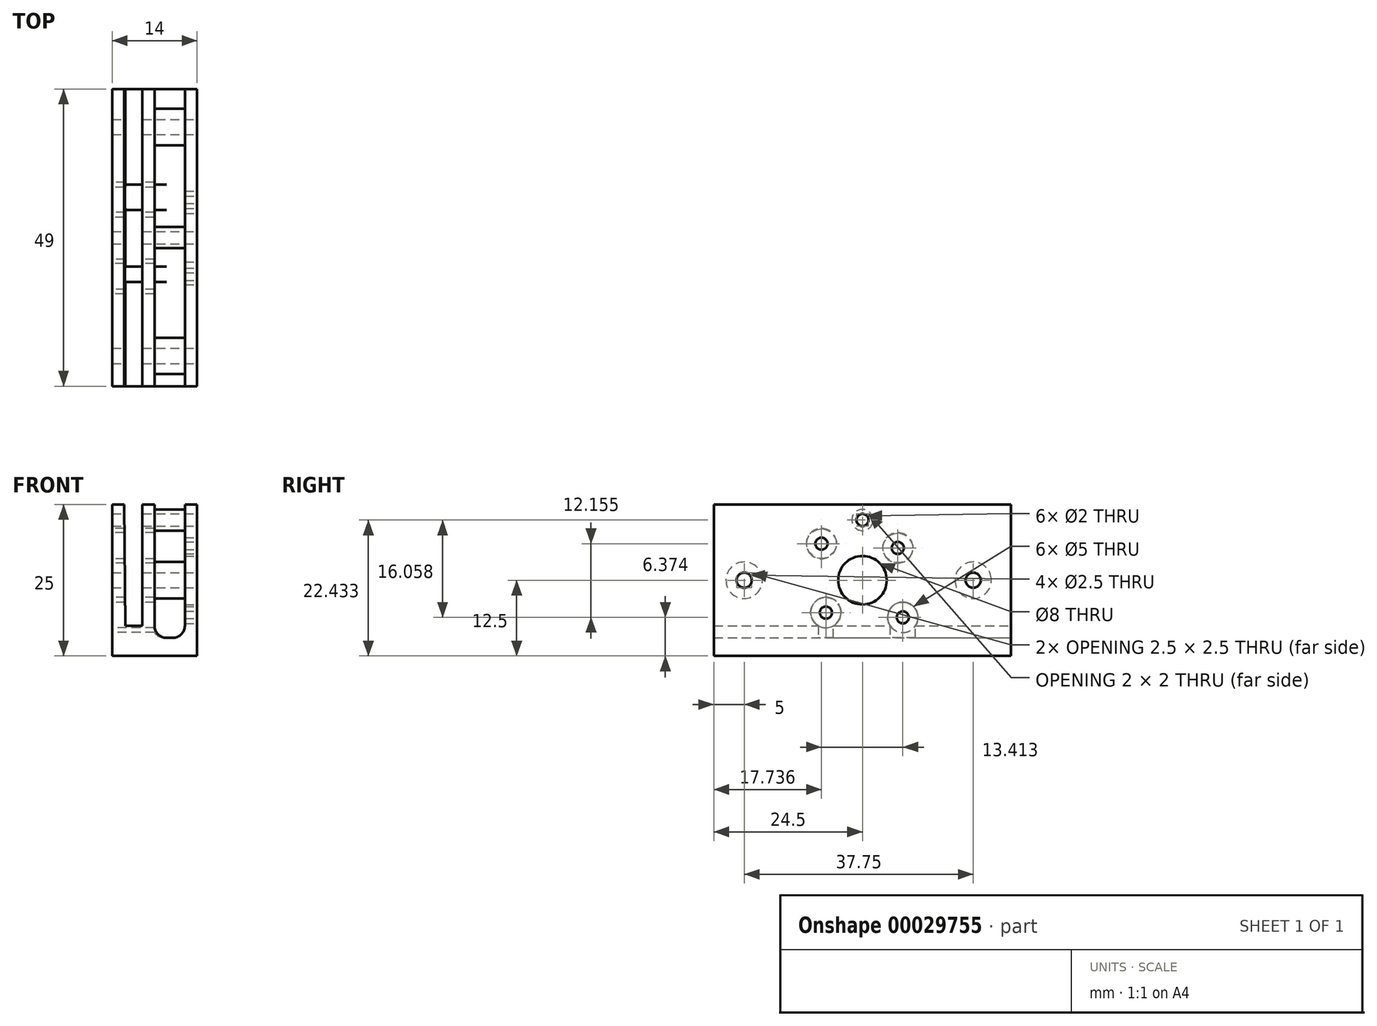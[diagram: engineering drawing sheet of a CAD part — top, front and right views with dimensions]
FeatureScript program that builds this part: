
annotation { "Feature Type Name" : "Feature", "Feature Type Description" : "" }
export const myFeature = defineFeature(function(context is Context, id is Id, definition is map)
    precondition{}
    {
        {
            var Q0;
            Q0=qCreatedBy(makeId("Front.planeOp"),FACE);
            var sketch = newSketch(context, id + "F0", { "sketchPlane" : qUnion([Q0])});
            skLineSegment(sketch, "E0.top", {"start": v(0, 16) * mm, "end": v(2, 16) * mm});
            skLineSegment(sketch, "E0.right", {"start": v(2.18, -4) * mm, "end": v(2, 16) * mm});
            skLineSegment(sketch, "E1", {"start": v(14, 0) * mm, "end": v(14, 16) * mm});
            skLineSegment(sketch, "E2", {"start": v(14, 16) * mm, "end": v(12, 16) * mm});
            skLineSegment(sketch, "E3", {"start": v(12, 16) * mm, "end": v(12, -6) * mm});
            skLineSegment(sketch, "E4", {"start": v(12, -6) * mm, "end": v(7, -6) * mm});
            skLineSegment(sketch, "E5", {"start": v(7, 16) * mm, "end": v(5, 16) * mm});
            skLineSegment(sketch, "E6", {"start": v(5, 16) * mm, "end": v(5, -4) * mm});
            skLineSegment(sketch, "E7", {"start": v(7, 16) * mm, "end": v(7, -6) * mm});
            skLineSegment(sketch, "E8", {"start": v(12, 0) * mm, "end": v(12, -6) * mm});
            skLineSegment(sketch, "E9", {"start": v(12, -9) * mm, "end": v(14, -9) * mm});
            skLineSegment(sketch, "E10", {"start": v(14, -9) * mm, "end": v(14, 0) * mm});
            skLineSegment(sketch, "E11", {"start": v(12, -9) * mm, "end": v(0, -9) * mm});
            skPoint(sketch, "E12.end.orphan", {"position": v(0, 0) * mm});
            skLineSegment(sketch, "E13", {"start": v(0, -9) * mm, "end": v(0, 16) * mm});
            skLineSegment(sketch, "E14", {"start": v(5, -4) * mm, "end": v(2.18, -4) * mm});
            skSolve(sketch);
        }
        {
            var Q0;
            Q0 = qSketchRegion(id + "F0", true);
            extrude(context, id + "F1", {"entities" : qUnion([Q0]), "depth" : 49 * mm});
        }
        {
            var Q0;
            Q0=makeQuery(id+"F1.opExtrude","SWEPT_FACE",FACE,{"disambiguationData":[OSD([sQuery(id+"F0.wireOp",EDGE,"E1"),sQuery(id+"F0.wireOp",EDGE,"E10")])]});
            var sketch = newSketch(context, id + "F2", { "sketchPlane" : qUnion([Q0])});
            skCircle(sketch, "E15", {"center": v(-18.67, 8.83) * mm, "radius": 1 * mm});
            skCircle(sketch, "E16", {"center": v(-17.85, -2.63) * mm, "radius": 1 * mm});
            skCircle(sketch, "E17", {"center": v(-30.54, -1.83) * mm, "radius": 1 * mm});
            skCircle(sketch, "E18", {"center": v(-31.26, 9.53) * mm, "radius": 1 * mm});
            skCircle(sketch, "E19", {"center": v(-24.5, 3.5) * mm, "radius": 4 * mm});
            skCircle(sketch, "E20", {"center": v(-44, 3.5) * mm, "radius": 1.25 * mm});
            skPoint(sketch, "E20.centerSnap0", {"position": v(-49, 3.5) * mm});
            skCircle(sketch, "E21", {"center": v(-6.25, 3.5) * mm, "radius": 1.25 * mm});
            skPoint(sketch, "E21.centerSnap0", {"position": v(0, 3.5) * mm});
            skCircle(sketch, "E22", {"center": v(-24.5, 13.43) * mm, "radius": 1 * mm});
            skSolve(sketch);
        }
        {
            var Q0;
            Q0=makeQuery(id+"F2.imprint","IMPRINT",FACE,{"disambiguationData":[TD([[makeQuery(id+"F2.imprint","IMPRINT",EDGE,{"derivedFrom":sQuery(id+"F2.wireOp",EDGE,"E18")}),1.0]])]});
            var Q1;
            Q1=makeQuery(id+"F2.imprint","IMPRINT",FACE,{"disambiguationData":[TD([[makeQuery(id+"F2.imprint","IMPRINT",EDGE,{"derivedFrom":sQuery(id+"F2.wireOp",EDGE,"E15")}),1.0]])]});
            var Q2;
            Q2=makeQuery(id+"F2.imprint","IMPRINT",FACE,{"disambiguationData":[TD([[makeQuery(id+"F2.imprint","IMPRINT",EDGE,{"derivedFrom":sQuery(id+"F2.wireOp",EDGE,"E16")}),1.0]])]});
            var Q3;
            Q3=makeQuery(id+"F2.imprint","IMPRINT",FACE,{"disambiguationData":[TD([[makeQuery(id+"F2.imprint","IMPRINT",EDGE,{"derivedFrom":sQuery(id+"F2.wireOp",EDGE,"E17")}),1.0]])]});
            var Q4;
            Q4=makeQuery(id+"F2.imprint","IMPRINT",FACE,{"disambiguationData":[TD([[makeQuery(id+"F2.imprint","IMPRINT",EDGE,{"derivedFrom":sQuery(id+"F2.wireOp",EDGE,"E21")}),1.0]])]});
            var Q5;
            Q5=makeQuery(id+"F2.imprint","IMPRINT",FACE,{"disambiguationData":[TD([[makeQuery(id+"F2.imprint","IMPRINT",EDGE,{"derivedFrom":sQuery(id+"F2.wireOp",EDGE,"E20")}),1.0]])]});
            var Q6;
            Q6=makeQuery(id+"F2.imprint","IMPRINT",FACE,{"disambiguationData":[TD([[makeQuery(id+"F2.imprint","IMPRINT",EDGE,{"derivedFrom":sQuery(id+"F2.wireOp",EDGE,"E22")}),1.0]])]});
            var Q7;
            Q7=makeQuery(id+"F1.opExtrude","SWEPT_FACE",FACE,{"disambiguationData":[OSD([sQuery(id+"F0.wireOp",EDGE,"E7")])]});
            extrude(context, id + "F3", {"entities" : qUnion([Q0, Q1, Q2, Q3, Q4, Q5, Q6]), "operationType" : NewBodyOperationType.REMOVE, "oppositeDirection" : true, "endBoundEntityFace" : qUnion([Q7]), "depth" : 25 * mm});
        }
        {
            var Q0;
            Q0=makeQuery(id+"F2.imprint","IMPRINT",FACE,{"disambiguationData":[TD([[makeQuery(id+"F2.imprint","IMPRINT",EDGE,{"derivedFrom":sQuery(id+"F2.wireOp",EDGE,"E18")}),1.0]])]});
            var Q1;
            Q1=makeQuery(id+"F2.imprint","IMPRINT",FACE,{"disambiguationData":[TD([[makeQuery(id+"F2.imprint","IMPRINT",EDGE,{"derivedFrom":sQuery(id+"F2.wireOp",EDGE,"E15")}),1.0]])]});
            var Q2;
            Q2=makeQuery(id+"F2.imprint","IMPRINT",FACE,{"disambiguationData":[TD([[makeQuery(id+"F2.imprint","IMPRINT",EDGE,{"derivedFrom":sQuery(id+"F2.wireOp",EDGE,"E16")}),1.0]])]});
            var Q3;
            Q3=makeQuery(id+"F2.imprint","IMPRINT",FACE,{"disambiguationData":[TD([[makeQuery(id+"F2.imprint","IMPRINT",EDGE,{"derivedFrom":sQuery(id+"F2.wireOp",EDGE,"E17")}),1.0]])]});
            var Q4;
            Q4=makeQuery(id+"F1.opExtrude","SWEPT_FACE",FACE,{"disambiguationData":[OSD([sQuery(id+"F0.wireOp",EDGE,"E0.right")])]});
            extrude(context, id + "F4", {"entities" : qUnion([Q0, Q1, Q2, Q3]), "operationType" : NewBodyOperationType.REMOVE, "oppositeDirection" : true, "endBoundEntityFace" : qUnion([Q4]), "depth" : 25 * mm});
        }
        {
            var Q0;
            Q0 = qSketchRegion(id + "F2", true);
            var Q1;
            Q1=makeQuery(id+"F1.opExtrude","SWEPT_FACE",FACE,{"disambiguationData":[OSD([sQuery(id+"F0.wireOp",EDGE,"E3")])]});
            extrude(context, id + "F5", {"entities" : qUnion([Q0]), "operationType" : NewBodyOperationType.REMOVE, "oppositeDirection" : true, "endBoundEntityFace" : qUnion([Q1]), "depth" : 3 * mm});
        }
        {
            var Q0;
            Q0=makeQuery(id+"F1.opExtrude","SWEPT_FACE",FACE,{"disambiguationData":[OSD([sQuery(id+"F0.wireOp",EDGE,"E13")])]});
            var sketch = newSketch(context, id + "F6", { "sketchPlane" : qUnion([Q0])});
            skCircle(sketch, "E23", {"center": v(18.67, 8.83) * mm, "radius": 2.5 * mm});
            skCircle(sketch, "E24", {"center": v(31.26, 9.53) * mm, "radius": 2.5 * mm});
            skCircle(sketch, "E25", {"center": v(30.54, -1.83) * mm, "radius": 2.5 * mm});
            skCircle(sketch, "E26", {"center": v(17.85, -2.63) * mm, "radius": 2.5 * mm});
            skSolve(sketch);
        }
        {
            var Q0;
            Q0 = qSketchRegion(id + "F6", true);
            var Q1;
            Q1=makeQuery(id+"F1.opExtrude","SWEPT_FACE",FACE,{"disambiguationData":[OSD([sQuery(id+"F0.wireOp",EDGE,"E7")])]});
            extrude(context, id + "F7", {"entities" : qUnion([Q0]), "operationType" : NewBodyOperationType.REMOVE, "endBound" : BoundingType.UP_TO_SURFACE, "oppositeDirection" : true, "endBoundEntityFace" : qUnion([Q1]), "depth" : 25 * mm});
        }
        {
            var Q0;
            Q0=makeQuery(id+"F1.opExtrude","SWEPT_EDGE",EDGE,{"disambiguationData":[OSD([sQuery(id+"F0.wireOp",EDGE,"E4"),sQuery(id+"F0.wireOp",EDGE,"E8")])]});
            var Q1;
            Q1=makeQuery(id+"F1.opExtrude","SWEPT_EDGE",EDGE,{"disambiguationData":[OSD([sQuery(id+"F0.wireOp",EDGE,"E4"),sQuery(id+"F0.wireOp",EDGE,"E7")])]});
            fillet(context, id + "F8", {"entities" : qUnion([Q0, Q1]), "radius" : 2 * mm, "tangentPropagation" : true, "allowEdgeOverflow" : false});
        }
        {
            var Q0;
            Q0=makeQuery(id+"F1.opExtrude","SWEPT_FACE",FACE,{"disambiguationData":[OSD([sQuery(id+"F0.wireOp",EDGE,"E1"),sQuery(id+"F0.wireOp",EDGE,"E10")])]});
            var sketch = newSketch(context, id + "F9", { "sketchPlane" : qUnion([Q0])});
            skCircle(sketch, "E27", {"center": v(-44, 3.5) * mm, "radius": 3 * mm});
            skCircle(sketch, "E28", {"center": v(-6.25, 3.5) * mm, "radius": 3 * mm});
            skCircle(sketch, "E29", {"center": v(-24.5, 13.43) * mm, "radius": 1.75 * mm});
            skSolve(sketch);
        }
        {
            var Q0;
            Q0=makeQuery(id+"F9.imprint","IMPRINT",FACE,{"disambiguationData":[TD([[makeQuery(id+"F9.imprint","IMPRINT",EDGE,{"derivedFrom":sQuery(id+"F9.wireOp",EDGE,"E27")}),1.0]])]});
            var Q1;
            Q1=makeQuery(id+"F9.imprint","IMPRINT",FACE,{"disambiguationData":[TD([[makeQuery(id+"F9.imprint","IMPRINT",EDGE,{"derivedFrom":sQuery(id+"F9.wireOp",EDGE,"E28")}),1.0]])]});
            var Q2;
            Q2=makeQuery(id+"F9.imprint","IMPRINT",FACE,{"disambiguationData":[TD([[makeQuery(id+"F9.imprint","IMPRINT",EDGE,{"derivedFrom":sQuery(id+"F9.wireOp",EDGE,"E29")}),1.0]])]});
            var Q3;
            Q3=makeQuery(id+"F1.opExtrude","SWEPT_FACE",FACE,{"disambiguationData":[OSD([sQuery(id+"F0.wireOp",EDGE,"E7")])]});
            extrude(context, id + "F10", {"entities" : qUnion([Q0, Q1, Q2]), "operationType" : NewBodyOperationType.ADD, "endBound" : BoundingType.UP_TO_SURFACE, "oppositeDirection" : true, "endBoundEntityFace" : qUnion([Q3]), "depth" : 25 * mm});
        }
    });
